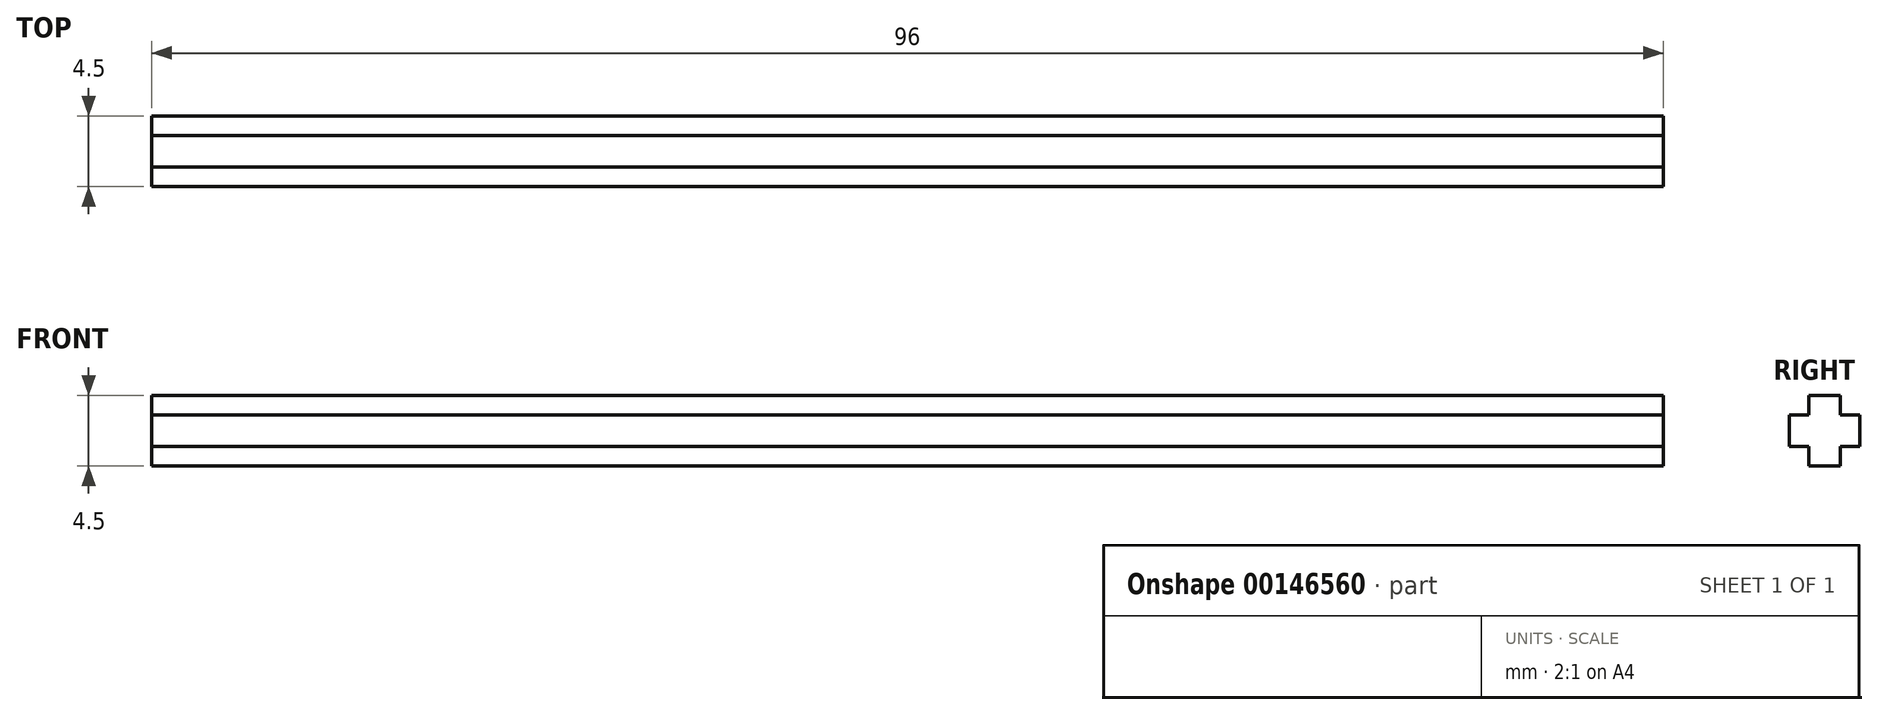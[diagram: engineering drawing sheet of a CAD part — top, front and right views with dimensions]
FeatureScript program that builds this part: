
annotation { "Feature Type Name" : "Feature", "Feature Type Description" : "" }
export const myFeature = defineFeature(function(context is Context, id is Id, definition is map)
    precondition{}
    {
        {
            var Q0;
            Q0=qCreatedBy(makeId("Front.planeOp"),FACE);
            var sketch = newSketch(context, id + "F0", { "sketchPlane" : qUnion([Q0])});
            skLineSegment(sketch, "E0", {"start": v(-48, 0) * mm, "end": v(48, 0) * mm});
            skSolve(sketch);
        }
        {
            var Q0;
            Q0=sQuery(id+"F0.wireOp",EDGE,"E0");
            var Q1;
            Q1=sQuery(id+"F0.wireOp",VERTEX,"E0.start");
            cPlane(context, id + "F1", {"entities" : qUnion([Q0, Q1]), "cplaneType" : CPlaneType.CURVE_POINT, "offset" : 25 * mm, "width" : 150 * mm, "height" : 150 * mm});
        }
        {
            var Q0;
            Q0=qCreatedBy(id+"F1.planeOp",FACE);
            var sketch = newSketch(context, id + "F2", { "sketchPlane" : qUnion([Q0])});
            skLineSegment(sketch, "E1.bottom", {"start": v(-1, -2.25) * mm, "end": v(1, -2.25) * mm});
            skLineSegment(sketch, "E1.top", {"start": v(-1, 2.25) * mm, "end": v(1, 2.25) * mm});
            skLineSegment(sketch, "E1.left", {"start": v(-1, -2.25) * mm, "end": v(-1, -1) * mm});
            skLineSegment(sketch, "E1.right", {"start": v(1, -2.25) * mm, "end": v(1, -1) * mm});
            skPoint(sketch, "E1.middle", {"position": v(0, 0) * mm});
            skLineSegment(sketch, "E2.bottom", {"start": v(-2.25, -1) * mm, "end": v(-1, -1) * mm});
            skLineSegment(sketch, "E2.top", {"start": v(-2.25, 1) * mm, "end": v(-1, 1) * mm});
            skLineSegment(sketch, "E2.left", {"start": v(-2.25, -1) * mm, "end": v(-2.25, 1) * mm});
            skLineSegment(sketch, "E2.right", {"start": v(2.25, -1) * mm, "end": v(2.25, 1) * mm});
            skLineSegment(sketch, "E3.trimOffspring", {"start": v(1, 1) * mm, "end": v(2.25, 1) * mm});
            skLineSegment(sketch, "E4.trimOffspring", {"start": v(1, 1) * mm, "end": v(1, 2.25) * mm});
            skLineSegment(sketch, "E5.trimOffspring", {"start": v(-1, 1) * mm, "end": v(-1, 2.25) * mm});
            skLineSegment(sketch, "E6.trimOffspring", {"start": v(1, -1) * mm, "end": v(2.25, -1) * mm});
            skSolve(sketch);
        }
        {
            var Q0;
            Q0=makeQuery(id+"F2.imprint","IMPRINT",FACE,{"disambiguationData":[TD([[makeQuery(id+"F2.imprint","IMPRINT",EDGE,{"derivedFrom":sQuery(id+"F2.wireOp",EDGE,"E1.bottom")}),1.0]])]});
            var Q1;
            Q1=sQuery(id+"F0.wireOp",EDGE,"E0");
            sweep(context, id + "F3", {"profiles" : qUnion([Q0]), "path" : qUnion([Q1])});
        }
    });
